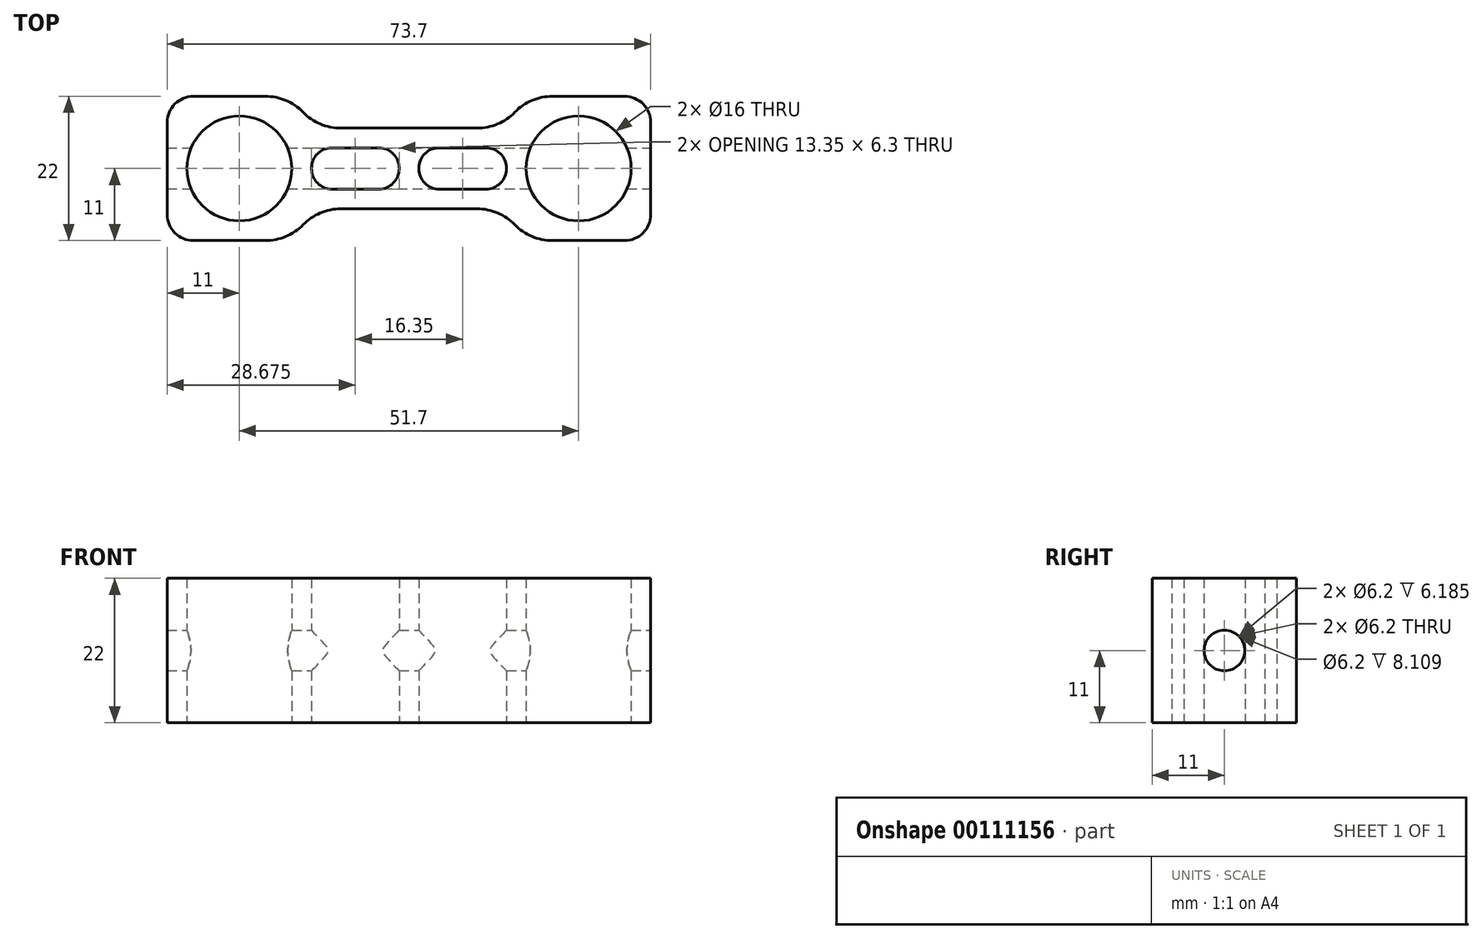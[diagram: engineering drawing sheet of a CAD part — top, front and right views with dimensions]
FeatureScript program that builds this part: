
annotation { "Feature Type Name" : "Feature", "Feature Type Description" : "" }
export const myFeature = defineFeature(function(context is Context, id is Id, definition is map)
    precondition{}
    {
        {
            var Q0;
            Q0=qCreatedBy(makeId("Top.planeOp"),FACE);
            var sketch = newSketch(context, id + "F0", { "sketchPlane" : qUnion([Q0])});
            skLineSegment(sketch, "E0.rect.bottom", {"start": v(36.85, -11) * mm, "end": v(17.85, -11) * mm});
            skLineSegment(sketch, "E0.rect.top", {"start": v(36.85, 11) * mm, "end": v(17.85, 11) * mm});
            skLineSegment(sketch, "E0.rect.left", {"start": v(36.85, -11) * mm, "end": v(36.85, 11) * mm});
            skPoint(sketch, "E0.rect.middle", {"position": v(0, 0) * mm});
            skCircle(sketch, "E1", {"center": v(25.85, 0) * mm, "radius": 8 * mm});
            skLineSegment(sketch, "E2", {"start": v(25.85, 0) * mm, "end": v(33.85, 0) * mm, "construction": true});
            skLineSegment(sketch, "E3", {"start": v(0, 0) * mm, "end": v(25.85, 0) * mm, "construction": true});
            skLineSegment(sketch, "E4", {"start": v(25.85, 0) * mm, "end": v(25.85, 8) * mm, "construction": true});
            skLineSegment(sketch, "E5.rect.bottom", {"start": v(14.85, 3.15) * mm, "end": v(0, 3.15) * mm});
            skLineSegment(sketch, "E5.rect.top", {"start": v(14.85, -3.15) * mm, "end": v(0, -3.15) * mm});
            skLineSegment(sketch, "E5.rect.left", {"start": v(14.85, 3.15) * mm, "end": v(14.85, -3.15) * mm});
            skPoint(sketch, "E6", {"position": v(17.85, 0) * mm});
            skPoint(sketch, "E7", {"position": v(14.85, 0) * mm});
            skLineSegment(sketch, "E8", {"start": v(0, 6.15) * mm, "end": v(14.85, 6.15) * mm});
            skLineSegment(sketch, "E9", {"start": v(14.85, 6.15) * mm, "end": v(17.85, 11) * mm});
            skLineSegment(sketch, "E10", {"start": v(0, 19.7) * mm, "end": v(0, -23.6) * mm, "construction": true});
            skPoint(sketch, "E11", {"position": v(0, 6.15) * mm});
            skLineSegment(sketch, "E12", {"start": v(0, -6.15) * mm, "end": v(14.85, -6.15) * mm});
            skLineSegment(sketch, "E13", {"start": v(14.85, -6.15) * mm, "end": v(17.85, -11) * mm});
            skLineSegment(sketch, "E14", {"start": v(17.85, 11) * mm, "end": v(0, 11) * mm, "construction": true});
            skLineSegment(sketch, "E15", {"start": v(17.85, -11) * mm, "end": v(0, -11) * mm, "construction": true});
            skLineSegment(sketch, "E16.1.MirrorCS", {"start": v(-14.85, 3.15) * mm, "end": v(-14.85, -3.15) * mm});
            skLineSegment(sketch, "E16.2.MirrorCS", {"start": v(-14.85, 6.15) * mm, "end": v(-17.85, 11) * mm});
            skLineSegment(sketch, "E16.4.MirrorCS", {"start": v(-36.85, -11) * mm, "end": v(-17.85, -11) * mm});
            skLineSegment(sketch, "E16.5.MirrorCS", {"start": v(-14.85, -6.15) * mm, "end": v(-17.85, -11) * mm});
            skLineSegment(sketch, "E16.6.MirrorCS", {"start": v(-17.85, -11) * mm, "end": v(0, -11) * mm, "construction": true});
            skPoint(sketch, "E16.7.MirrorP", {"position": v(-17.85, 0) * mm});
            skPoint(sketch, "E16.8.MirrorP", {"position": v(-14.85, 0) * mm});
            skLineSegment(sketch, "E16.9.MirrorCS", {"start": v(-25.85, 0) * mm, "end": v(-25.85, 8) * mm, "construction": true});
            skLineSegment(sketch, "E16.10.MirrorCS", {"start": v(-14.85, -3.15) * mm, "end": v(0, -3.15) * mm});
            skCircle(sketch, "E16.11.MirrorC", {"center": v(-25.85, 0) * mm, "radius": 8 * mm});
            skLineSegment(sketch, "E16.13.MirrorCS", {"start": v(0, -6.15) * mm, "end": v(-14.85, -6.15) * mm});
            skLineSegment(sketch, "E16.14.MirrorCS", {"start": v(-14.85, 3.15) * mm, "end": v(0, 3.15) * mm});
            skLineSegment(sketch, "E16.15.MirrorCS", {"start": v(-36.85, 11) * mm, "end": v(-17.85, 11) * mm});
            skLineSegment(sketch, "E16.16.MirrorCS", {"start": v(-25.85, 0) * mm, "end": v(-33.85, 0) * mm, "construction": true});
            skLineSegment(sketch, "E16.17.MirrorCS", {"start": v(0, 6.15) * mm, "end": v(-14.85, 6.15) * mm});
            skLineSegment(sketch, "E16.18.MirrorCS", {"start": v(-17.85, 11) * mm, "end": v(0, 11) * mm, "construction": true});
            skLineSegment(sketch, "E16.19.MirrorCS", {"start": v(0, 0) * mm, "end": v(-25.85, 0) * mm, "construction": true});
            skLineSegment(sketch, "E16.20.MirrorCS", {"start": v(-36.85, -11) * mm, "end": v(-36.85, 11) * mm});
            skLineSegment(sketch, "E17.rect.bottom", {"start": v(-1.5, 3.15) * mm, "end": v(1.5, 3.15) * mm});
            skLineSegment(sketch, "E17.rect.top", {"start": v(-1.5, -3.15) * mm, "end": v(1.5, -3.15) * mm});
            skLineSegment(sketch, "E17.rect.left", {"start": v(-1.5, 3.15) * mm, "end": v(-1.5, -3.15) * mm});
            skLineSegment(sketch, "E17.rect.right", {"start": v(1.5, 3.15) * mm, "end": v(1.5, -3.15) * mm});
            skSolve(sketch);
        }
        {
            var Q0;
            Q0=qSketchRegion(id+"F0",true);
            var Q1;
            {var subQ1=sQuery(id+"F0.wireOp",EDGE,"E17.rect.left");Q1=makeQuery(id+"F0.imprint","IMPRINT",FACE,{"disambiguationData":[TD([[makeQuery(id+"F0.imprint","IMPRINT",EDGE,{"derivedFrom":subQ1}),1.0]])]});}
            extrude(context, id + "F1", {"entities" : qUnion([Q0, Q1]), "depth" : 22 * mm});
        }
        {
            var Q0;
            Q0=makeQuery(id+"F1.opExtrude","SWEPT_EDGE",EDGE,{"disambiguationData":[OSD([sQuery(id+"F0.wireOp",EDGE,"E0.rect.bottom"),sQuery(id+"F0.wireOp",EDGE,"E0.rect.left")])]});
            var Q1;
            Q1=makeQuery(id+"F1.opExtrude","SWEPT_EDGE",EDGE,{"disambiguationData":[OSD([sQuery(id+"F0.wireOp",EDGE,"E0.rect.top"),sQuery(id+"F0.wireOp",EDGE,"E0.rect.left")])]});
            var Q2;
            Q2=makeQuery(id+"F1.opExtrude","SWEPT_EDGE",EDGE,{"disambiguationData":[OSD([sQuery(id+"F0.wireOp",EDGE,"E16.15.MirrorCS"),sQuery(id+"F0.wireOp",EDGE,"E16.20.MirrorCS")])]});
            var Q3;
            Q3=makeQuery(id+"F1.opExtrude","SWEPT_EDGE",EDGE,{"disambiguationData":[OSD([sQuery(id+"F0.wireOp",EDGE,"E16.4.MirrorCS"),sQuery(id+"F0.wireOp",EDGE,"E16.20.MirrorCS")])]});
            fillet(context, id + "F2", {"entities" : qUnion([Q0, Q1, Q2, Q3]), "radius" : 4 * mm, "tangentPropagation" : true, "allowEdgeOverflow" : false});
        }
        {
            var Q0;
            Q0=makeQuery(id+"F1.opExtrude","SWEPT_EDGE",EDGE,{"disambiguationData":[OSD([sQuery(id+"F0.wireOp",EDGE,"E16.1.MirrorCS"),sQuery(id+"F0.wireOp",EDGE,"E16.14.MirrorCS")])]});
            var Q1;
            Q1=makeQuery(id+"F1.opExtrude","SWEPT_EDGE",EDGE,{"disambiguationData":[OSD([sQuery(id+"F0.wireOp",EDGE,"E5.rect.bottom"),sQuery(id+"F0.wireOp",EDGE,"E5.rect.left")])]});
            var Q2;
            Q2=makeQuery(id+"F1.opExtrude","SWEPT_EDGE",EDGE,{"disambiguationData":[OSD([sQuery(id+"F0.wireOp",EDGE,"E5.rect.top"),sQuery(id+"F0.wireOp",EDGE,"E5.rect.left")])]});
            var Q3;
            Q3=makeQuery(id+"F1.opExtrude","SWEPT_EDGE",EDGE,{"disambiguationData":[OSD([sQuery(id+"F0.wireOp",EDGE,"E16.1.MirrorCS"),sQuery(id+"F0.wireOp",EDGE,"E16.10.MirrorCS")])]});
            var Q4;
            Q4=makeQuery(id+"F1.opExtrude","SWEPT_EDGE",EDGE,{"disambiguationData":[OSD([sQuery(id+"F0.wireOp",EDGE,"E5.rect.bottom"),sQuery(id+"F0.wireOp",EDGE,"E17.rect.bottom"),sQuery(id+"F0.wireOp",EDGE,"E17.rect.right")])]});
            var Q5;
            Q5=makeQuery(id+"F1.opExtrude","SWEPT_EDGE",EDGE,{"disambiguationData":[OSD([sQuery(id+"F0.wireOp",EDGE,"E16.14.MirrorCS"),sQuery(id+"F0.wireOp",EDGE,"E17.rect.bottom"),sQuery(id+"F0.wireOp",EDGE,"E17.rect.left")])]});
            var Q6;
            Q6=makeQuery(id+"F1.opExtrude","SWEPT_EDGE",EDGE,{"disambiguationData":[OSD([sQuery(id+"F0.wireOp",EDGE,"E16.10.MirrorCS"),sQuery(id+"F0.wireOp",EDGE,"E17.rect.top"),sQuery(id+"F0.wireOp",EDGE,"E17.rect.left")])]});
            var Q7;
            Q7=makeQuery(id+"F1.opExtrude","SWEPT_EDGE",EDGE,{"disambiguationData":[OSD([sQuery(id+"F0.wireOp",EDGE,"E5.rect.top"),sQuery(id+"F0.wireOp",EDGE,"E17.rect.top"),sQuery(id+"F0.wireOp",EDGE,"E17.rect.right")])]});
            fillet(context, id + "F3", {"entities" : qUnion([Q0, Q1, Q2, Q3, Q4, Q5, Q6, Q7]), "radius" : 3.1 * mm, "tangentPropagation" : true, "allowEdgeOverflow" : false});
        }
        {
            var Q0;
            Q0=makeQuery(id+"F1.opExtrude","SWEPT_EDGE",EDGE,{"disambiguationData":[OSD([sQuery(id+"F0.wireOp",EDGE,"E16.2.MirrorCS"),sQuery(id+"F0.wireOp",EDGE,"E16.17.MirrorCS")])]});
            var Q1;
            Q1=makeQuery(id+"F1.opExtrude","SWEPT_EDGE",EDGE,{"disambiguationData":[OSD([sQuery(id+"F0.wireOp",EDGE,"E8"),sQuery(id+"F0.wireOp",EDGE,"E9")])]});
            var Q2;
            Q2=makeQuery(id+"F1.opExtrude","SWEPT_EDGE",EDGE,{"disambiguationData":[OSD([sQuery(id+"F0.wireOp",EDGE,"E16.5.MirrorCS"),sQuery(id+"F0.wireOp",EDGE,"E16.13.MirrorCS")])]});
            var Q3;
            Q3=makeQuery(id+"F1.opExtrude","SWEPT_EDGE",EDGE,{"disambiguationData":[OSD([sQuery(id+"F0.wireOp",EDGE,"E12"),sQuery(id+"F0.wireOp",EDGE,"E13")])]});
            fillet(context, id + "F4", {"entities" : qUnion([Q0, Q1, Q2, Q3]), "radius" : 8 * mm, "tangentPropagation" : true, "allowEdgeOverflow" : false});
        }
        {
            var Q0;
            Q0=makeQuery(id+"F1.opExtrude","SWEPT_EDGE",EDGE,{"disambiguationData":[OSD([sQuery(id+"F0.wireOp",EDGE,"E0.rect.bottom"),sQuery(id+"F0.wireOp",EDGE,"E13")])]});
            var Q1;
            Q1=makeQuery(id+"F1.opExtrude","SWEPT_EDGE",EDGE,{"disambiguationData":[OSD([sQuery(id+"F0.wireOp",EDGE,"E16.4.MirrorCS"),sQuery(id+"F0.wireOp",EDGE,"E16.5.MirrorCS")])]});
            var Q2;
            Q2=makeQuery(id+"F1.opExtrude","SWEPT_EDGE",EDGE,{"disambiguationData":[OSD([sQuery(id+"F0.wireOp",EDGE,"E16.2.MirrorCS"),sQuery(id+"F0.wireOp",EDGE,"E16.15.MirrorCS")])]});
            var Q3;
            Q3=makeQuery(id+"F1.opExtrude","SWEPT_EDGE",EDGE,{"disambiguationData":[OSD([sQuery(id+"F0.wireOp",EDGE,"E0.rect.top"),sQuery(id+"F0.wireOp",EDGE,"E9")])]});
            fillet(context, id + "F5", {"entities" : qUnion([Q0, Q1, Q2, Q3]), "radius" : 8 * mm, "tangentPropagation" : true, "allowEdgeOverflow" : false});
        }
        {
            var Q0;
            Q0=makeQuery(id+"F1.opExtrude","SWEPT_FACE",FACE,{"disambiguationData":[OSD([sQuery(id+"F0.wireOp",EDGE,"E0.rect.left")])]});
            var sketch = newSketch(context, id + "F6", { "sketchPlane" : qUnion([Q0])});
            skCircle(sketch, "E18", {"center": v(0, 11) * mm, "radius": 3.1 * mm});
            skLineSegment(sketch, "E19", {"start": v(7, 22) * mm, "end": v(-7, 0) * mm, "construction": true});
            skSolve(sketch);
        }
        {
            var Q0;
            Q0=qSketchRegion(id+"F6",true);
            extrude(context, id + "F7", {"entities" : qUnion([Q0]), "operationType" : NewBodyOperationType.REMOVE, "endBound" : BoundingType.THROUGH_ALL, "oppositeDirection" : true, "depth" : 25 * mm});
        }
    });
